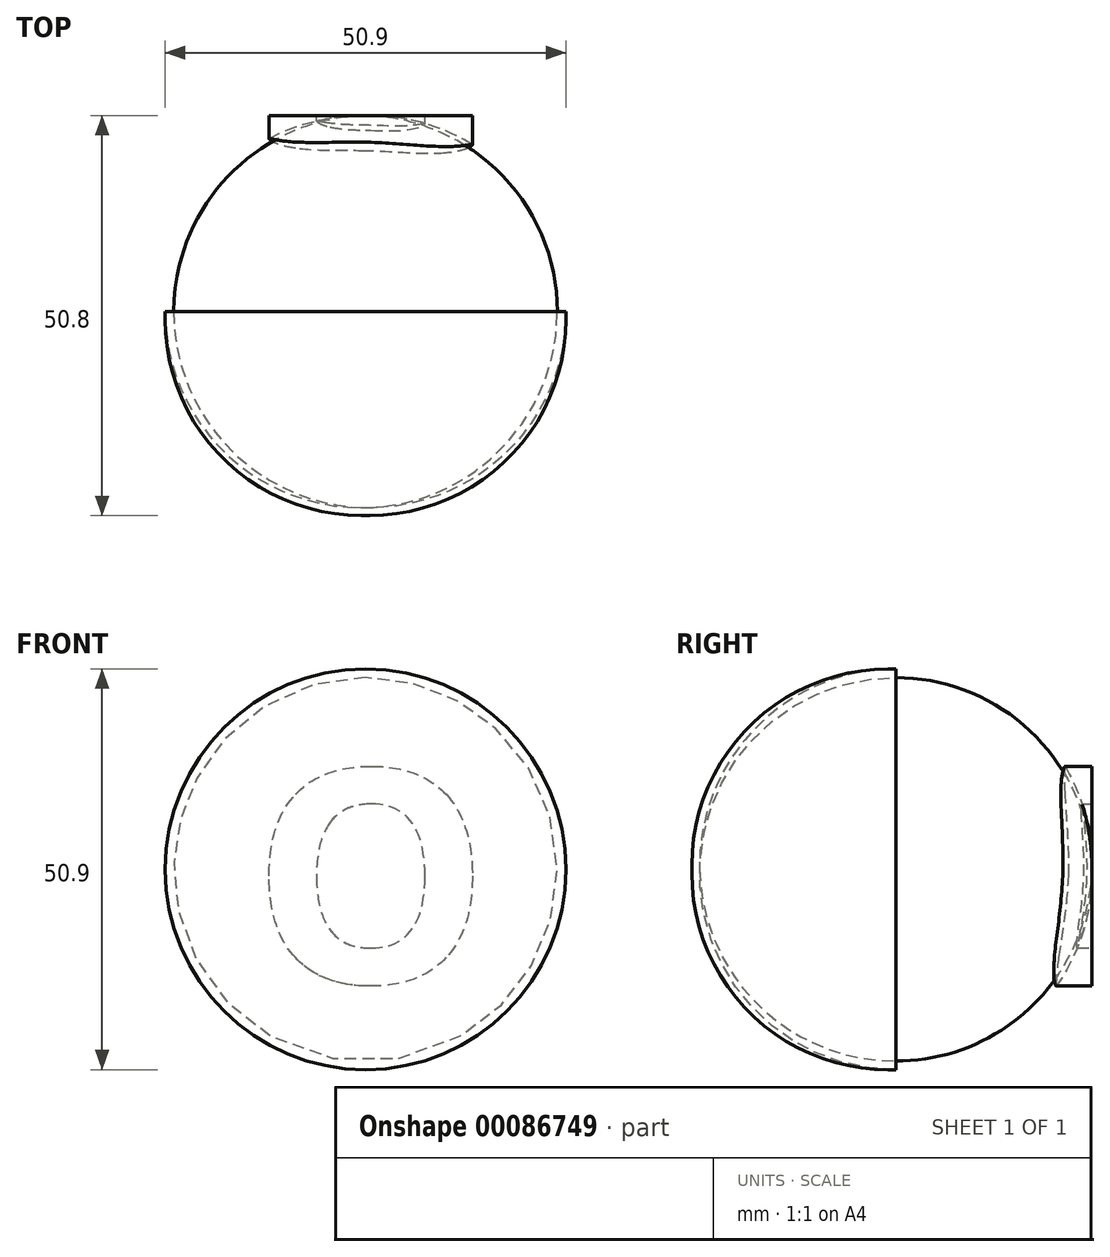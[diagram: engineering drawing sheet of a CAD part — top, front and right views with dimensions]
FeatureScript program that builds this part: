
annotation { "Feature Type Name" : "Feature", "Feature Type Description" : "" }
export const myFeature = defineFeature(function(context is Context, id is Id, definition is map)
    precondition{}
    {
        {
            var Q0;
            Q0=qCreatedBy(makeId("Front.planeOp"),FACE);
            var sketch = newSketch(context, id + "F0", { "sketchPlane" : qUnion([Q0])});
            skCircle(sketch, "E0", {"center": v(-26.29, 24.26) * mm, "radius": 25.45 * mm});
            skText(sketch, "E1", { "text": "O", "fontName": "OpenSans-Bold.ttf"});
            const initialGuessF0  = {"E1": [-0.04146, 0.01014, 1, 0, 0.02805]};
            skSetInitialGuess(sketch, initialGuessF0);
            skSolve(sketch);
        }
        {
            var Q0;
            Q0=makeQuery(id+"F0.imprint","IMPRINT",FACE,{"disambiguationData":[TD([[makeQuery(id+"F0.imprint","IMPRINT",EDGE,{"derivedFrom":sQuery(id+"F0.wireOp",EDGE,"E1.sketch_text.stroke-8")}),1.0]])]});
            var Q1;
            Q1=makeQuery(id+"F0.imprint","IMPRINT",FACE,{"disambiguationData":[TD([[makeQuery(id+"F0.imprint","IMPRINT",EDGE,{"derivedFrom":sQuery(id+"F0.wireOp",EDGE,"E1.sketch_text.stroke-0")}),-1.0]])]});
            var Q2;
            Q2=makeQuery(id+"F0.imprint","IMPRINT",FACE,{"disambiguationData":[TD([[makeQuery(id+"F0.imprint","IMPRINT",EDGE,{"derivedFrom":sQuery(id+"F0.wireOp",EDGE,"E0")}),1.0]])]});
            extrude(context, id + "F1", {"entities" : qUnion([Q0, Q1, Q2]), "depth" : 50.8 * mm});
        }
        {
            var Q0;
            Q0=makeQuery(id+"F1.opExtrude","CAP_EDGE",EDGE,{"disambiguationData":[OSD([sQuery(id+"F0.wireOp",EDGE,"E0")])],"isStart":true});
            var Q1;
            Q1=makeQuery(id+"F1.opExtrude","CAP_EDGE",EDGE,{"disambiguationData":[OSD([sQuery(id+"F0.wireOp",EDGE,"E0")])],"isStart":false});
            fillet(context, id + "F2", {"entities" : qUnion([Q0, Q1]), "radius" : 24.9 * mm, "tangentPropagation" : true, "allowEdgeOverflow" : false});
        }
        {
            var Q0;
            Q0=qCreatedBy(makeId("Front.planeOp"),FACE);
            var sketch = newSketch(context, id + "F3", { "sketchPlane" : qUnion([Q0])});
            skText(sketch, "E2", { "text": "O", "fontName": "OpenSans-Bold.ttf"});
            const initialGuessF3  = {"E2": [-0.04075, 0.0098, 1, 0, 0.02735]};
            skSetInitialGuess(sketch, initialGuessF3);
            skSolve(sketch);
        }
        {
            var Q0;
            Q0=makeQuery(id+"F3.imprint","IMPRINT",FACE,{"disambiguationData":[TD([[makeQuery(id+"F3.imprint","IMPRINT",EDGE,{"derivedFrom":sQuery(id+"F3.wireOp",EDGE,"E2.sketch_text.stroke-0")}),-1.0]])]});
            extrude(context, id + "F4", {"entities" : qUnion([Q0]), "operationType" : NewBodyOperationType.ADD, "depth" : 12.7 * mm});
        }
    });
